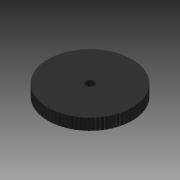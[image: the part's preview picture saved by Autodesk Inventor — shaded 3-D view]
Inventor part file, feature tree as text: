
AUTODESK INVENTOR PART (.ipt)
format: ipt  version: 2014 (Build 180170000, 170)  size: 397,312 bytes
history: native  units: in
note: dims shown in document units (in); Inventor stores cm internally (conversion verified against a paired STEP export)
features: other x3, sketch x3
ambient origin geometry x8: Origin, YZ Plane, XZ Plane, XY Plane, X Axis, Y Axis, Z Axis, Center Point
bodies: Solid1 (feature_tree)
feature tree (6):
  other  "wheel 1.ipt"
  other  "Solid1::wheel 1.ipt"
  other  "TaggingFeature1"
  sketch  "Sketch1"  dims[d0=0.3937in]
  sketch  "Sketch2"  dims[d1=0.3937in d2=0.0in d3=0.2756in d4=0.3937in d5=0.0in d7=0.3937in d8=0.0in d9=31.4961in d10=360.0deg]
  sketch  "Sketch3"
